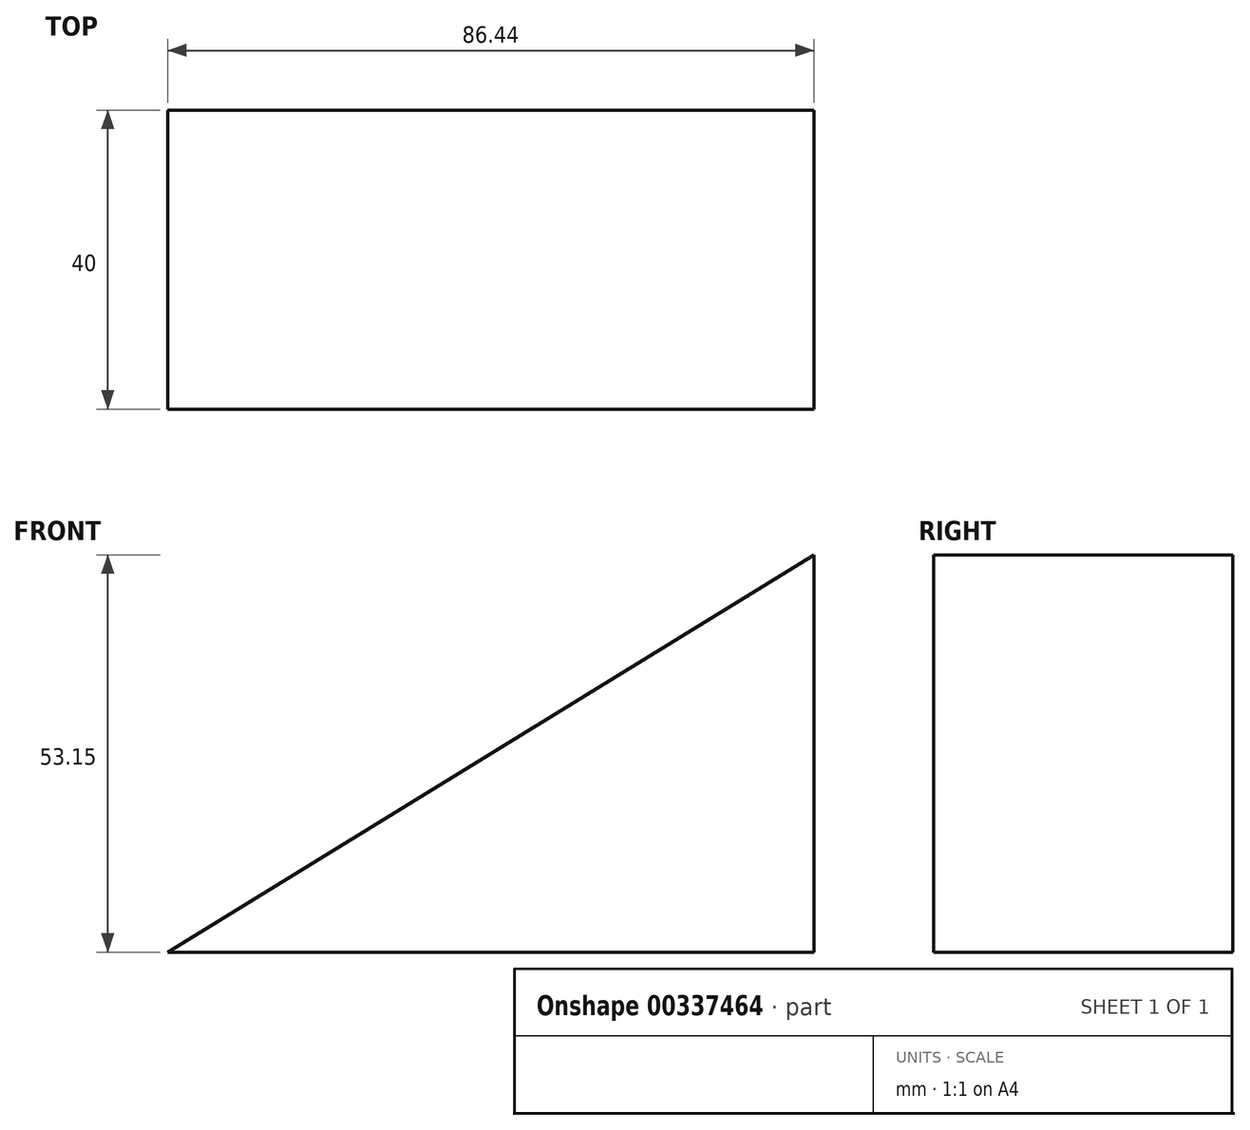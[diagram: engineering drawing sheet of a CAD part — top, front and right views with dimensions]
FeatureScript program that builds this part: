
annotation { "Feature Type Name" : "Feature", "Feature Type Description" : "" }
export const myFeature = defineFeature(function(context is Context, id is Id, definition is map)
    precondition{}
    {
        {
            var Q0;
            Q0=qCreatedBy(makeId("Front.planeOp"),FACE);
            var sketch = newSketch(context, id + "F0", { "sketchPlane" : qUnion([Q0])});
            skLineSegment(sketch, "E0", {"start": v(0, 0) * mm, "end": v(0, 53.15) * mm});
            skLineSegment(sketch, "E1", {"start": v(0, 53.15) * mm, "end": v(-86.44, 0) * mm});
            skLineSegment(sketch, "E2", {"start": v(-86.44, 0) * mm, "end": v(0, 0) * mm});
            skSolve(sketch);
        }
        {
            var Q0;
            Q0 = qSketchRegion(id + "F0", true);
            extrude(context, id + "F1", {"entities" : qUnion([Q0]), "depth" : 40 * mm});
        }
    });
